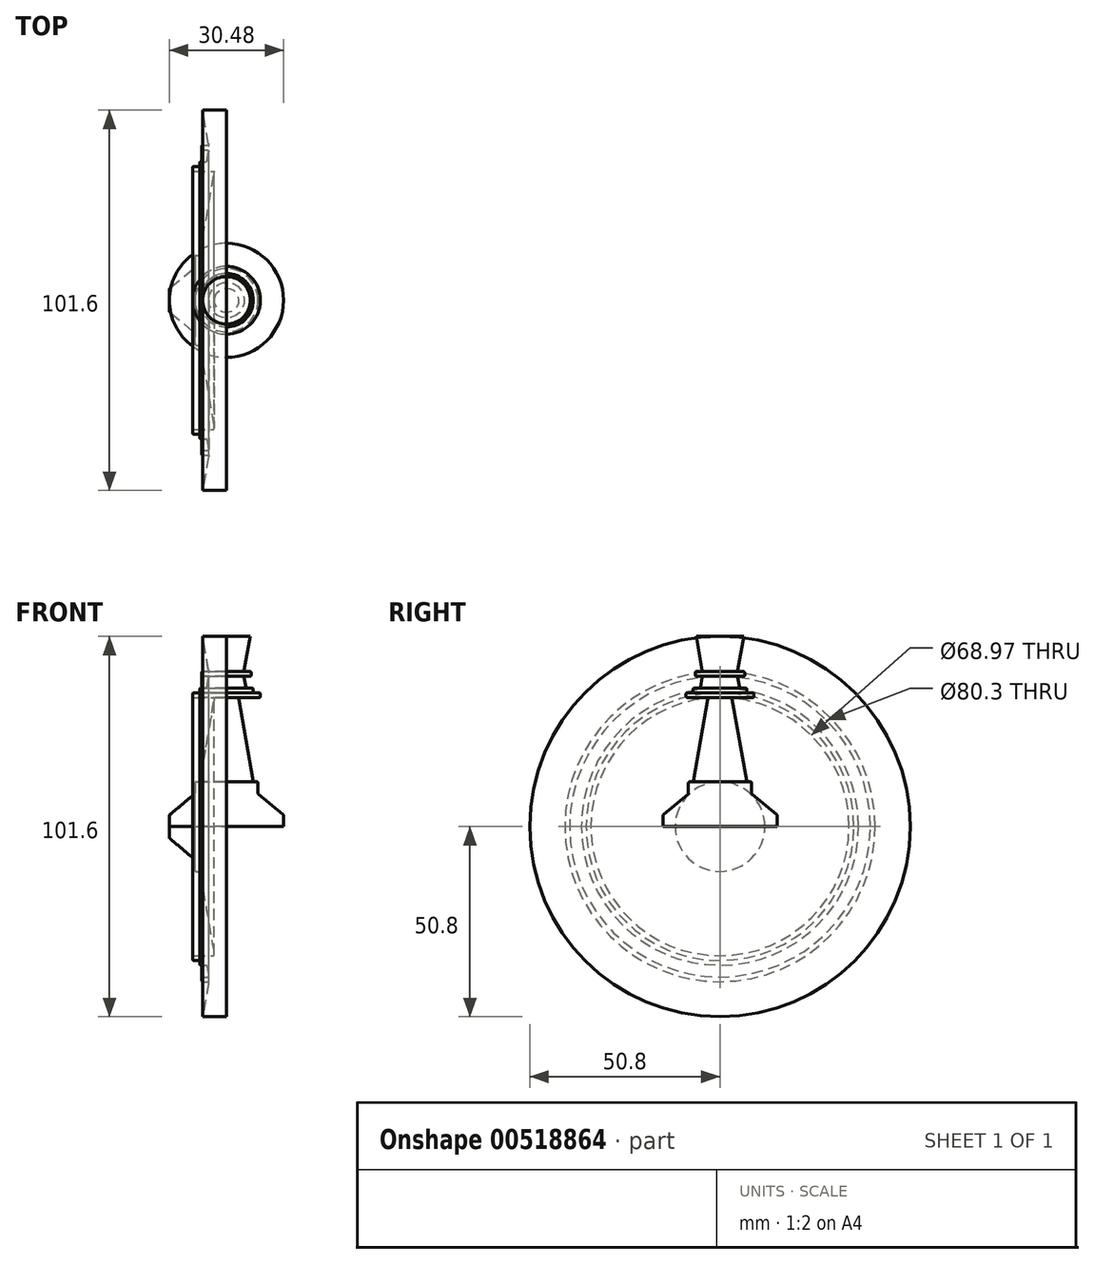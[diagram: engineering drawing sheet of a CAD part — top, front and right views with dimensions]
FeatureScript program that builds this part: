
annotation { "Feature Type Name" : "Feature", "Feature Type Description" : "" }
export const myFeature = defineFeature(function(context is Context, id is Id, definition is map)
    precondition{}
    {
        {
            var Q0;
            Q0=qCreatedBy(makeId("Front.planeOp"),FACE);
            var sketch = newSketch(context, id + "F0", { "sketchPlane" : qUnion([Q0])});
            skLineSegment(sketch, "E0.bottom", {"start": v(0, 0) * mm, "end": v(-15.24, 0) * mm});
            skLineSegment(sketch, "E0.top", {"start": v(0, 50.8) * mm, "end": v(-6.35, 50.8) * mm});
            skLineSegment(sketch, "E0.left", {"start": v(0, 0) * mm, "end": v(0, 50.8) * mm});
            skLineSegment(sketch, "E1", {"start": v(-15.24, 0) * mm, "end": v(-15.24, 2.93) * mm});
            skLineSegment(sketch, "E2", {"start": v(-15.13, 3.18) * mm, "end": v(-8.54, 8.7) * mm});
            skLineSegment(sketch, "E3", {"start": v(-8.43, 8.94) * mm, "end": v(-8.43, 11.65) * mm});
            skLineSegment(sketch, "E4", {"start": v(-8.11, 11.97) * mm, "end": v(-7.43, 11.97) * mm});
            skLineSegment(sketch, "E5", {"start": v(-7.11, 12.23) * mm, "end": v(-3.26, 34.11) * mm});
            skLineSegment(sketch, "E6", {"start": v(-3.57, 34.48) * mm, "end": v(-8.74, 34.48) * mm});
            skLineSegment(sketch, "E7", {"start": v(-9.06, 34.8) * mm, "end": v(-9.06, 35.44) * mm});
            skLineSegment(sketch, "E8", {"start": v(-8.74, 35.75) * mm, "end": v(-7.47, 35.75) * mm});
            skLineSegment(sketch, "E9", {"start": v(-7.15, 36.07) * mm, "end": v(-7.15, 36.7) * mm});
            skLineSegment(sketch, "E10", {"start": v(-6.83, 37.02) * mm, "end": v(-5.51, 37.02) * mm});
            skLineSegment(sketch, "E11", {"start": v(-5.2, 37.29) * mm, "end": v(-4.76, 39.78) * mm});
            skLineSegment(sketch, "E12", {"start": v(-5.07, 40.15) * mm, "end": v(-6.28, 40.15) * mm});
            skLineSegment(sketch, "E13", {"start": v(-6.6, 40.47) * mm, "end": v(-6.6, 41.1) * mm});
            skLineSegment(sketch, "E14", {"start": v(-6.28, 41.42) * mm, "end": v(-5.07, 41.42) * mm});
            skLineSegment(sketch, "E15", {"start": v(-4.76, 41.8) * mm, "end": v(-6.35, 50.8) * mm});
            skPoint(sketch, "E16.visualSharp", {"position": v(-15.24, 3.08) * mm});
            skArc(sketch, "E16.filletArc", {"start": v(-15.13, 3.18) * mm, "mid": v(-15.21, 3.07) * mm, "end": v(-15.24, 2.93) * mm});
            skPoint(sketch, "E17.visualSharp", {"position": v(-8.43, 8.8) * mm});
            skArc(sketch, "E17.filletArc", {"start": v(-8.54, 8.7) * mm, "mid": v(-8.46, 8.8) * mm, "end": v(-8.43, 8.94) * mm});
            skPoint(sketch, "E18.visualSharp", {"position": v(-3.2, 34.48) * mm});
            skArc(sketch, "E18.filletArc", {"start": v(-3.26, 34.11) * mm, "mid": v(-3.33, 34.37) * mm, "end": v(-3.57, 34.48) * mm});
            skPoint(sketch, "E19.visualSharp", {"position": v(-8.43, 11.97) * mm});
            skArc(sketch, "E19.filletArc", {"start": v(-8.11, 11.97) * mm, "mid": v(-8.34, 11.88) * mm, "end": v(-8.43, 11.65) * mm});
            skPoint(sketch, "E20.visualSharp", {"position": v(-7.16, 11.97) * mm});
            skArc(sketch, "E20.filletArc", {"start": v(-7.43, 11.97) * mm, "mid": v(-7.22, 12.04) * mm, "end": v(-7.11, 12.23) * mm});
            skPoint(sketch, "E21.visualSharp", {"position": v(-9.06, 34.48) * mm});
            skArc(sketch, "E21.filletArc", {"start": v(-9.06, 34.8) * mm, "mid": v(-8.96, 34.58) * mm, "end": v(-8.74, 34.48) * mm});
            skPoint(sketch, "E22.visualSharp", {"position": v(-9.06, 35.75) * mm});
            skArc(sketch, "E22.filletArc", {"start": v(-8.74, 35.75) * mm, "mid": v(-8.96, 35.66) * mm, "end": v(-9.06, 35.44) * mm});
            skPoint(sketch, "E23.visualSharp", {"position": v(-7.15, 35.75) * mm});
            skArc(sketch, "E23.filletArc", {"start": v(-7.47, 35.75) * mm, "mid": v(-7.25, 35.85) * mm, "end": v(-7.15, 36.07) * mm});
            skPoint(sketch, "E24.visualSharp", {"position": v(-7.15, 37.02) * mm});
            skArc(sketch, "E24.filletArc", {"start": v(-6.83, 37.02) * mm, "mid": v(-7.06, 36.93) * mm, "end": v(-7.15, 36.7) * mm});
            skPoint(sketch, "E25.visualSharp", {"position": v(-5.25, 37.02) * mm});
            skArc(sketch, "E25.filletArc", {"start": v(-5.51, 37.02) * mm, "mid": v(-5.3, 37.1) * mm, "end": v(-5.2, 37.29) * mm});
            skPoint(sketch, "E26.visualSharp", {"position": v(-4.7, 40.15) * mm});
            skArc(sketch, "E26.filletArc", {"start": v(-4.76, 39.78) * mm, "mid": v(-4.83, 40.04) * mm, "end": v(-5.07, 40.15) * mm});
            skPoint(sketch, "E27.visualSharp", {"position": v(-6.6, 40.15) * mm});
            skArc(sketch, "E27.filletArc", {"start": v(-6.6, 40.47) * mm, "mid": v(-6.5, 40.24) * mm, "end": v(-6.28, 40.15) * mm});
            skPoint(sketch, "E28.visualSharp", {"position": v(-6.6, 41.42) * mm});
            skArc(sketch, "E28.filletArc", {"start": v(-6.28, 41.42) * mm, "mid": v(-6.5, 41.33) * mm, "end": v(-6.6, 41.1) * mm});
            skPoint(sketch, "E29.visualSharp", {"position": v(-4.7, 41.42) * mm});
            skArc(sketch, "E29.filletArc", {"start": v(-5.07, 41.42) * mm, "mid": v(-4.83, 41.53) * mm, "end": v(-4.76, 41.8) * mm});
            skSolve(sketch);
        }
        {
            var Q0;
            Q0=makeQuery(id+"F0.imprint","IMPRINT",FACE,{"disambiguationData":[TD([[makeQuery(id+"F0.imprint","IMPRINT",EDGE,{"derivedFrom":sQuery(id+"F0.wireOp",EDGE,"E0.bottom")}),-1.0]])]});
            var Q1;
            Q1=sQuery(id+"F0.wireOp",EDGE,"E0.left");
            var Q2;
            Q2=sQuery(id+"F0.wireOp",EDGE,"E0.bottom");
            revolve(context, id + "F1", {"entities" : qUnion([Q0]), "surfaceEntities" : qUnion([Q1]), "axis" : qUnion([Q2]), "revolveType" : RevolveType.FULL});
        }
        {
            var Q0;
            Q0=makeQuery(id+"F0.imprint","IMPRINT",FACE,{"disambiguationData":[TD([[makeQuery(id+"F0.imprint","IMPRINT",EDGE,{"derivedFrom":sQuery(id+"F0.wireOp",EDGE,"E0.bottom")}),-1.0]])]});
            var Q1;
            Q1=sQuery(id+"F0.wireOp",EDGE,"E0.left");
            revolve(context, id + "F2", {"entities" : qUnion([Q0]), "axis" : qUnion([Q1]), "revolveType" : RevolveType.FULL});
        }
    });
